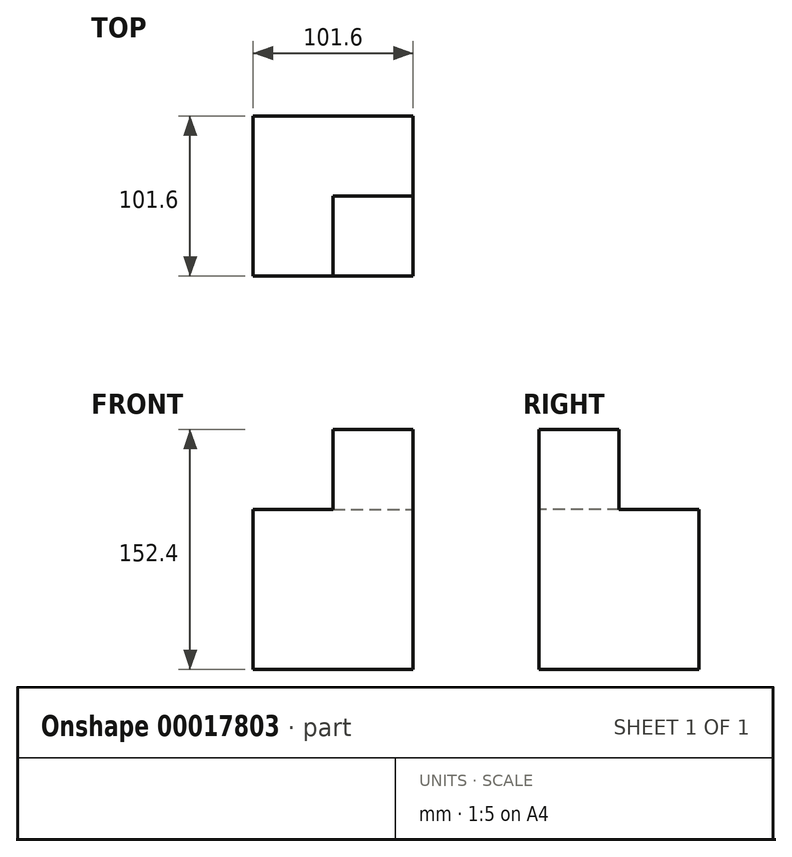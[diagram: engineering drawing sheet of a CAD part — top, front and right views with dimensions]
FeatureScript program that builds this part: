
annotation { "Feature Type Name" : "Feature", "Feature Type Description" : "" }
export const myFeature = defineFeature(function(context is Context, id is Id, definition is map)
    precondition{}
    {
        {
            var Q0;
            Q0=qCreatedBy(makeId("Front.planeOp"),FACE);
            var sketch = newSketch(context, id + "F0", { "sketchPlane" : qUnion([Q0])});
            skLineSegment(sketch, "E0.rect.bottom", {"start": v(50.8, 50.8) * mm, "end": v(-50.8, 50.8) * mm});
            skLineSegment(sketch, "E0.rect.top", {"start": v(50.8, -50.8) * mm, "end": v(-50.8, -50.8) * mm});
            skLineSegment(sketch, "E0.rect.left", {"start": v(50.8, 50.8) * mm, "end": v(50.8, -50.8) * mm});
            skLineSegment(sketch, "E0.rect.right", {"start": v(-50.8, 50.8) * mm, "end": v(-50.8, -50.8) * mm});
            skPoint(sketch, "E0.rect.middle", {"position": v(0, 0) * mm});
            skSolve(sketch);
        }
        {
            var Q0;
            Q0=makeQuery(id+"F0.imprint","IMPRINT",FACE,{"disambiguationData":[TD([[makeQuery(id+"F0.imprint","IMPRINT",EDGE,{"derivedFrom":sQuery(id+"F0.wireOp",EDGE,"E0.rect.bottom")}),1.0]])]});
            extrude(context, id + "F1", {"entities" : qUnion([Q0]), "endBound" : BoundingType.SYMMETRIC, "depth" : 101.6 * mm});
        }
        {
            var Q0;
            Q0=makeQuery(id+"F1.opExtrude","SWEPT_FACE",FACE,{"disambiguationData":[OSD([sQuery(id+"F0.wireOp",EDGE,"E0.rect.bottom")])]});
            var sketch = newSketch(context, id + "F2", { "sketchPlane" : qUnion([Q0])});
            skLineSegment(sketch, "E1.bottom", {"start": v(0, 0) * mm, "end": v(50.8, 0) * mm});
            skLineSegment(sketch, "E1.top", {"start": v(0, -50.8) * mm, "end": v(50.8, -50.8) * mm});
            skLineSegment(sketch, "E1.left", {"start": v(0, 0) * mm, "end": v(0, -50.8) * mm});
            skLineSegment(sketch, "E1.right", {"start": v(50.8, 0) * mm, "end": v(50.8, -50.8) * mm});
            skSolve(sketch);
        }
        {
            var Q0;
            Q0 = qSketchRegion(id + "F2", true);
            extrude(context, id + "F3", {"entities" : qUnion([Q0]), "operationType" : NewBodyOperationType.ADD, "depth" : 50.8 * mm});
        }
    });
